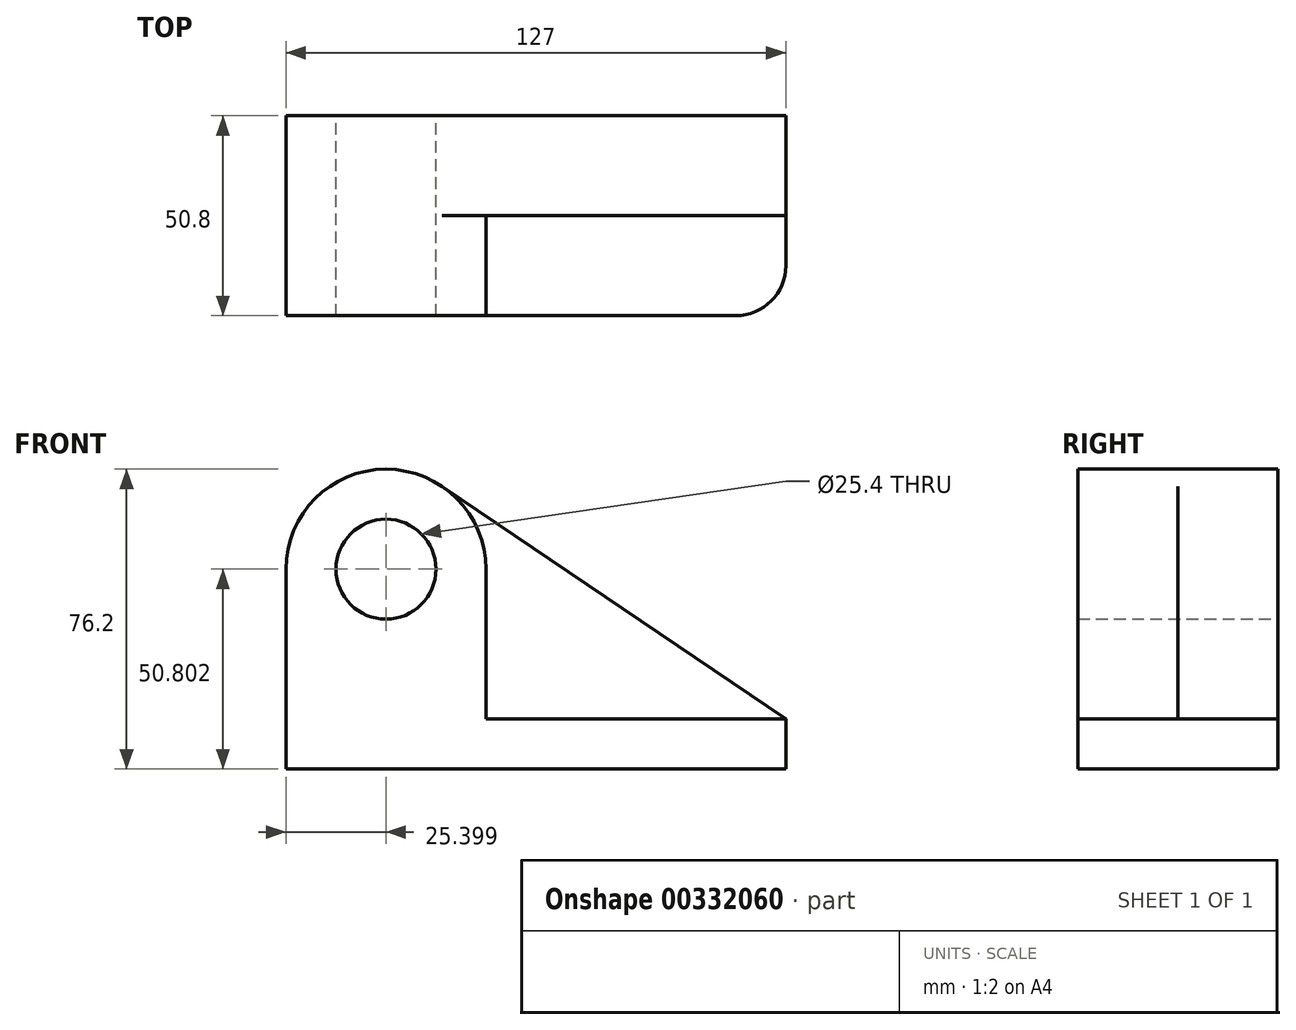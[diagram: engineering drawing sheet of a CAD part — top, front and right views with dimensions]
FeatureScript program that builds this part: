
annotation { "Feature Type Name" : "Feature", "Feature Type Description" : "" }
export const myFeature = defineFeature(function(context is Context, id is Id, definition is map)
    precondition{}
    {
        {
            var Q0;
            Q0=qCreatedBy(makeId("Front.planeOp"),FACE);
            var sketch = newSketch(context, id + "F0", { "sketchPlane" : qUnion([Q0])});
            skCircle(sketch, "E0", {"center": v(-175.2, 85.52) * mm, "radius": 12.7 * mm});
            skArc(sketch, "E1", {"start": v(-160.95, 106.56) * mm, "mid": v(-187.1, 107.96) * mm, "end": v(-200.6, 85.52) * mm});
            skLineSegment(sketch, "E2", {"start": v(-200.6, 85.52) * mm, "end": v(-200.6, 34.72) * mm});
            skLineSegment(sketch, "E3", {"start": v(-73.6, 34.72) * mm, "end": v(-200.6, 34.72) * mm});
            skLineSegment(sketch, "E4", {"start": v(-73.6, 47.42) * mm, "end": v(-73.6, 34.72) * mm});
            skLineSegment(sketch, "E5", {"start": v(-73.6, 47.42) * mm, "end": v(-160.95, 106.56) * mm});
            skSolve(sketch);
        }
        {
            var Q0;
            Q0=makeQuery(id+"F0.imprint","IMPRINT",FACE,{"disambiguationData":[TD([[makeQuery(id+"F0.imprint","IMPRINT",EDGE,{"derivedFrom":sQuery(id+"F0.wireOp",EDGE,"E0")}),-1.0]])]});
            extrude(context, id + "F1", {"entities" : qUnion([Q0]), "depth" : 25.4 * mm});
        }
        {
            var Q0;
            Q0=makeQuery(id+"F1.opExtrude","CAP_FACE",FACE,{"disambiguationData":[OSD([sQuery(id+"F0.wireOp",EDGE,"E0"),sQuery(id+"F0.wireOp",EDGE,"E1"),sQuery(id+"F0.wireOp",EDGE,"E2"),sQuery(id+"F0.wireOp",EDGE,"E3"),sQuery(id+"F0.wireOp",EDGE,"E4"),sQuery(id+"F0.wireOp",EDGE,"E5")])],"isStart":false});
            var sketch = newSketch(context, id + "F2", { "sketchPlane" : qUnion([Q0])});
            skCircle(sketch, "E6", {"center": v(-175.2, 85.52) * mm, "radius": 12.7 * mm});
            skLineSegment(sketch, "E7.bottom", {"start": v(-73.6, 47.42) * mm, "end": v(-149.8, 47.42) * mm});
            skLineSegment(sketch, "E7.top", {"start": v(-73.6, 34.72) * mm, "end": v(-200.6, 34.72) * mm});
            skLineSegment(sketch, "E7.left", {"start": v(-73.6, 47.42) * mm, "end": v(-73.6, 34.72) * mm});
            skLineSegment(sketch, "E7.right", {"start": v(-200.6, 47.42) * mm, "end": v(-200.6, 34.72) * mm});
            skArc(sketch, "E8", {"start": v(-149.8, 85.52) * mm, "mid": v(-175.2, 110.92) * mm, "end": v(-200.6, 85.52) * mm});
            skLineSegment(sketch, "E9", {"start": v(-149.8, 85.52) * mm, "end": v(-149.8, 47.42) * mm});
            skLineSegment(sketch, "E10", {"start": v(-200.6, 85.52) * mm, "end": v(-200.6, 47.42) * mm});
            skSolve(sketch);
        }
        {
            var Q0;
            Q0=makeQuery(id+"F2.imprint","IMPRINT",FACE,{"disambiguationData":[TD([[makeQuery(id+"F2.imprint","IMPRINT",EDGE,{"derivedFrom":sQuery(id+"F2.wireOp",EDGE,"E6")}),-1.0]])]});
            extrude(context, id + "F3", {"entities" : qUnion([Q0]), "operationType" : NewBodyOperationType.ADD, "depth" : 25.4 * mm});
        }
        {
            var Q0;
            Q0=makeQuery(id+"F3.opExtrude","CAP_EDGE",EDGE,{"disambiguationData":[OSD([sQuery(id+"F2.wireOp",EDGE,"E7.left")])],"isStart":false});
            fillet(context, id + "F4", {"entities" : qUnion([Q0]), "radius" : 12.7 * mm, "tangentPropagation" : true, "allowEdgeOverflow" : false});
        }
    });
